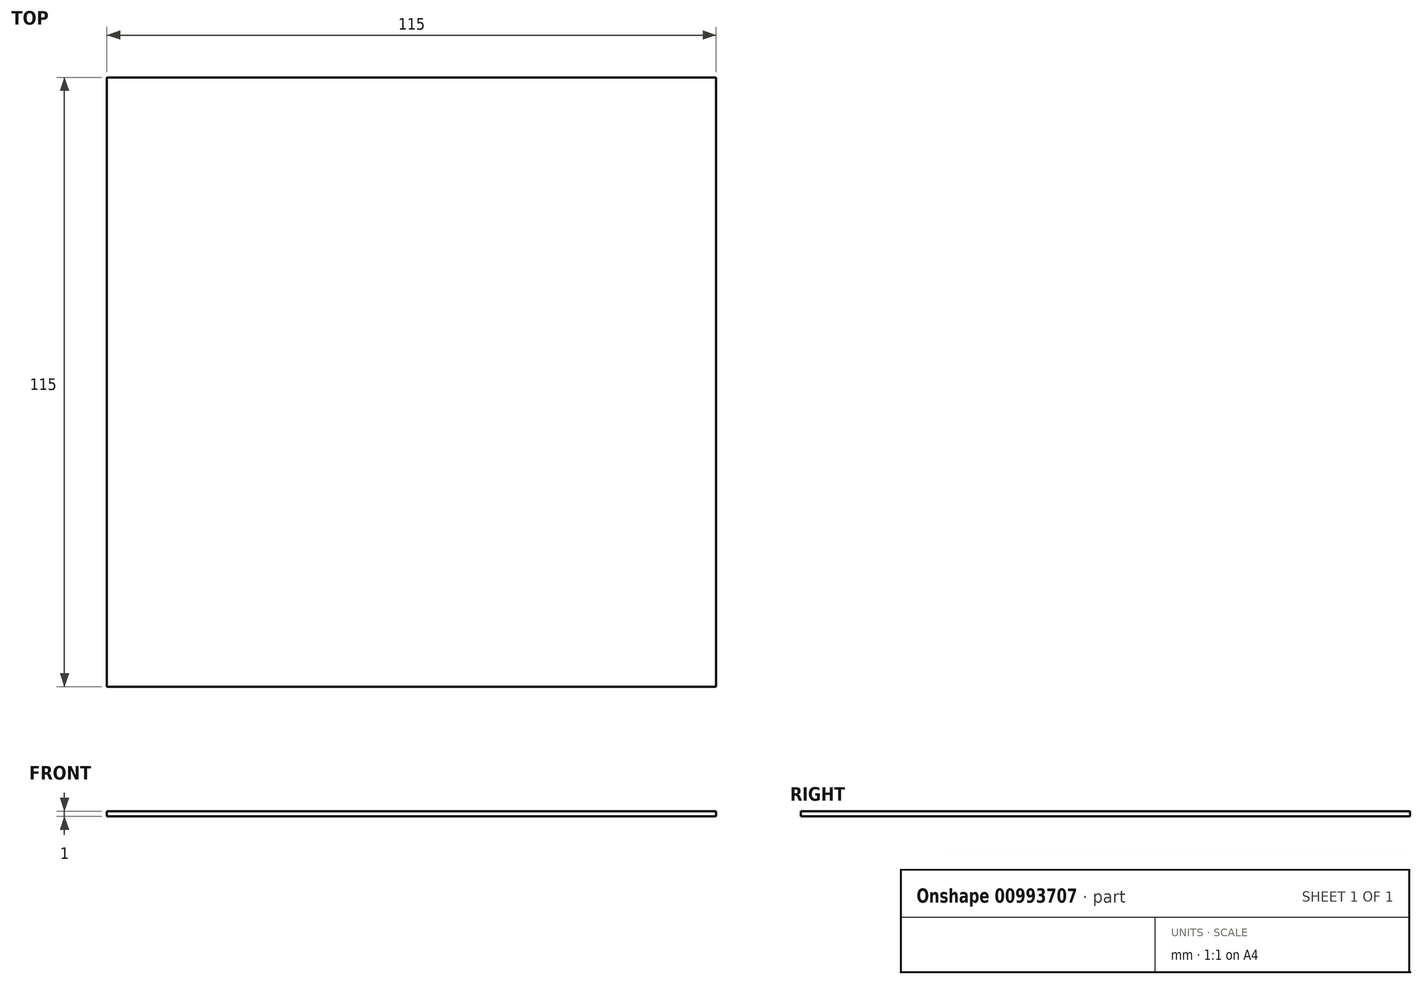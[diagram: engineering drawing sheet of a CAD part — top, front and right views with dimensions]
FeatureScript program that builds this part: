
annotation { "Feature Type Name" : "Feature", "Feature Type Description" : "" }
export const myFeature = defineFeature(function(context is Context, id is Id, definition is map)
    precondition{}
    {
        {
            var Q0;
            Q0=qCreatedBy(makeId("Top.planeOp"),FACE);
            cPlane(context, id + "F0", {"entities" : qUnion([Q0]), "cplaneType" : CPlaneType.OFFSET, "offset" : 30 * mm, "width" : 150 * mm, "height" : 150 * mm});
        }
        {
            var Q0;
            Q0=qCreatedBy(id+"F0.planeOp",FACE);
            var sketch = newSketch(context, id + "F1", { "sketchPlane" : qUnion([Q0])});
            skLineSegment(sketch, "E0.bottom", {"start": v(-57.5, 57.5) * mm, "end": v(57.5, 57.5) * mm});
            skLineSegment(sketch, "E0.top", {"start": v(-57.5, -57.5) * mm, "end": v(57.5, -57.5) * mm});
            skLineSegment(sketch, "E0.left", {"start": v(-57.5, 57.5) * mm, "end": v(-57.5, -57.5) * mm});
            skLineSegment(sketch, "E0.right", {"start": v(57.5, 57.5) * mm, "end": v(57.5, -57.5) * mm});
            skPoint(sketch, "E0.middle", {"position": v(0, 0) * mm});
            skSolve(sketch);
        }
        {
            var Q0;
            Q0=makeQuery(id+"F1.imprint","IMPRINT",FACE,{"disambiguationData":[TD([[makeQuery(id+"F1.imprint","IMPRINT",EDGE,{"derivedFrom":sQuery(id+"F1.wireOp",EDGE,"E0.bottom")}),-1.0]])]});
            extrude(context, id + "F2", {"entities" : qUnion([Q0]), "depth" : 1 * mm, "offsetDistance" : 25 * mm});
        }
    });
